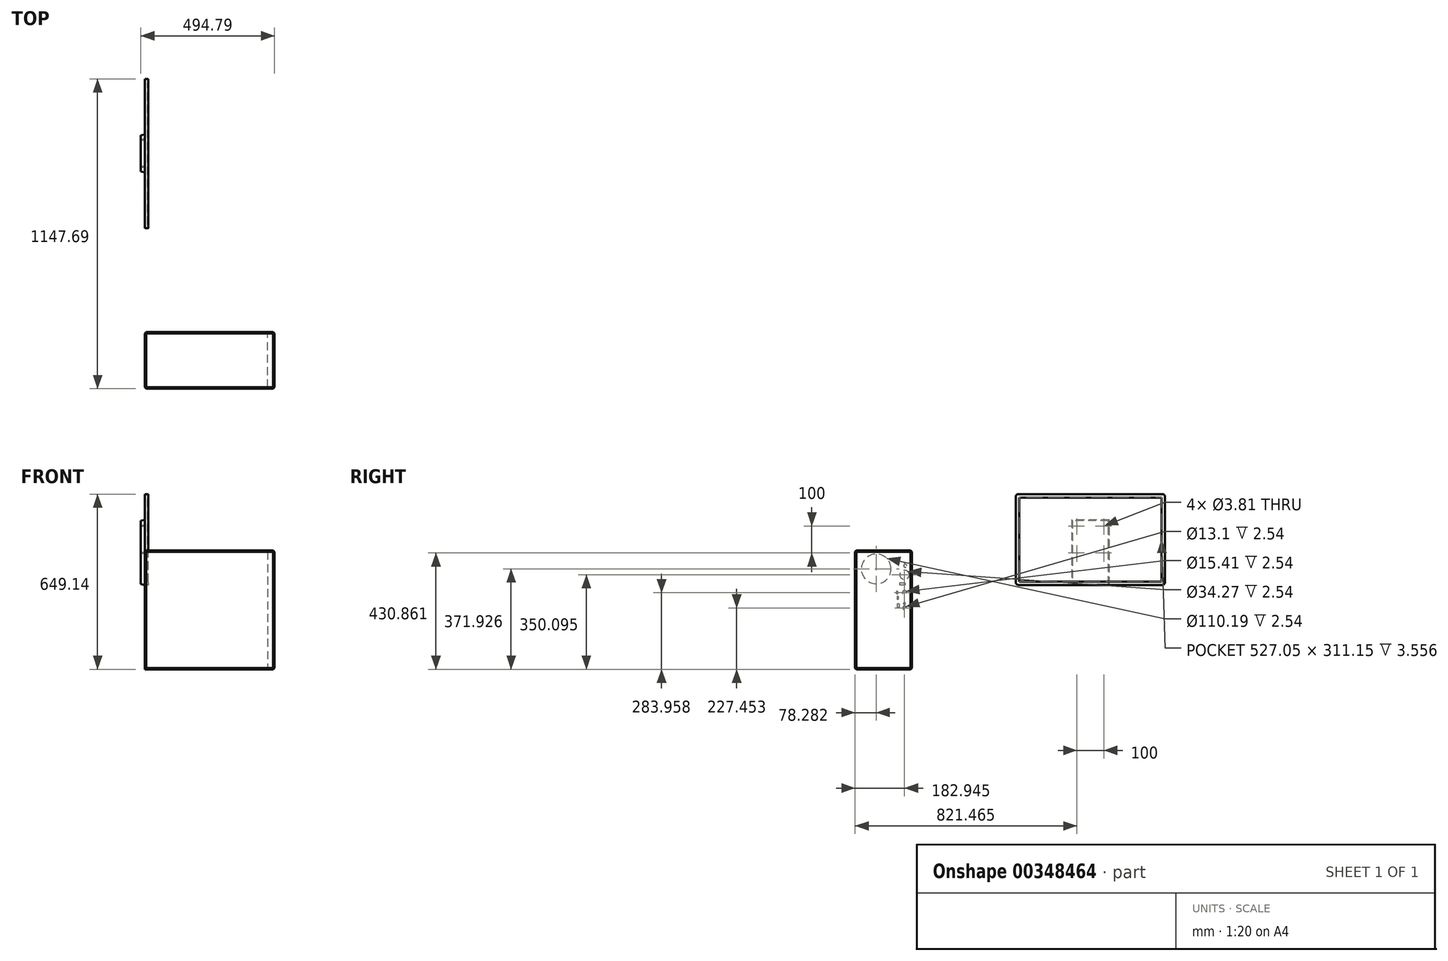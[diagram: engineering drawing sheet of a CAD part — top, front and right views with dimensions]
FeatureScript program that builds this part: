
annotation { "Feature Type Name" : "Feature", "Feature Type Description" : "" }
export const myFeature = defineFeature(function(context is Context, id is Id, definition is map)
    precondition{}
    {
        {
            var Q0;
            Q0=qCreatedBy(makeId("Top.planeOp"),FACE);
            var sketch = newSketch(context, id + "F0", { "sketchPlane" : qUnion([Q0])});
            skLineSegment(sketch, "E0.bottom", {"start": v(0, 0) * mm, "end": v(479.55, 0) * mm});
            skLineSegment(sketch, "E0.top", {"start": v(0, -210.06) * mm, "end": v(479.55, -210.06) * mm});
            skLineSegment(sketch, "E0.left", {"start": v(0, 0) * mm, "end": v(0, -210.06) * mm});
            skLineSegment(sketch, "E0.right", {"start": v(479.55, 0) * mm, "end": v(479.55, -210.06) * mm});
            skPoint(sketch, "E1", {"position": v(0, 0) * mm});
            skSolve(sketch);
        }
        {
            var Q0;
            Q0 = qSketchRegion(id + "F0", true);
            extrude(context, id + "F1", {"entities" : qUnion([Q0]), "depth" : 439.93 * mm});
        }
        {
            var Q0;
            Q0=makeQuery(id+"F1.opExtrude","CAP_FACE",FACE,{"disambiguationData":[OSD([sQuery(id+"F0.wireOp",EDGE,"E0.bottom"),sQuery(id+"F0.wireOp",EDGE,"E0.top"),sQuery(id+"F0.wireOp",EDGE,"E0.left"),sQuery(id+"F0.wireOp",EDGE,"E0.right")])],"isStart":false});
            var Q1;
            Q1=makeQuery(id+"F1.opExtrude","SWEPT_FACE",FACE,{"disambiguationData":[OSD([sQuery(id+"F0.wireOp",EDGE,"E0.top")])]});
            var Q2;
            Q2=makeQuery(id+"F1.opExtrude","SWEPT_FACE",FACE,{"disambiguationData":[OSD([sQuery(id+"F0.wireOp",EDGE,"E0.right")])]});
            var Q3;
            Q3=makeQuery(id+"F1.opExtrude","SWEPT_FACE",FACE,{"disambiguationData":[OSD([sQuery(id+"F0.wireOp",EDGE,"E0.bottom")])]});
            chamfer(context, id + "F2", {"entities" : qUnion([Q0, Q1, Q2, Q3]), "width" : 5.08 * mm, "tangentPropagation" : true});
        }
        {
            var Q0;
            Q0=makeQuery(id+"F1.opExtrude","SWEPT_FACE",FACE,{"disambiguationData":[OSD([sQuery(id+"F0.wireOp",EDGE,"E0.left")])]});
            var sketch = newSketch(context, id + "F3", { "sketchPlane" : qUnion([Q0])});
            skCircle(sketch, "E2", {"center": v(24.55, 383.48) * mm, "radius": 5.74 * mm});
            skCircle(sketch, "E3", {"center": v(27.12, 350.1) * mm, "radius": 17.13 * mm});
            skCircle(sketch, "E4", {"center": v(27.12, 283.96) * mm, "radius": 7.7 * mm});
            skCircle(sketch, "E5", {"center": v(27.12, 243.5) * mm, "radius": 3.9 * mm});
            skCircle(sketch, "E6", {"center": v(27.12, 227.45) * mm, "radius": 6.55 * mm});
            skLineSegment(sketch, "E7.bottom", {"start": v(24.55, 319.92) * mm, "end": v(45.1, 319.92) * mm});
            skLineSegment(sketch, "E7.top", {"start": v(24.55, 312.21) * mm, "end": v(45.1, 312.21) * mm});
            skLineSegment(sketch, "E7.left", {"start": v(24.55, 319.92) * mm, "end": v(24.55, 312.21) * mm});
            skLineSegment(sketch, "E7.right", {"start": v(45.1, 319.92) * mm, "end": v(45.1, 312.21) * mm});
            skLineSegment(sketch, "E8.bottom", {"start": v(53.44, 289.74) * mm, "end": v(57.3, 289.74) * mm});
            skLineSegment(sketch, "E8.top", {"start": v(53.44, 279.46) * mm, "end": v(57.3, 279.46) * mm});
            skLineSegment(sketch, "E8.left", {"start": v(53.44, 289.74) * mm, "end": v(53.44, 279.46) * mm});
            skLineSegment(sketch, "E8.right", {"start": v(57.3, 289.74) * mm, "end": v(57.3, 279.46) * mm});
            skLineSegment(sketch, "E9.bottom", {"start": v(50.23, 269.83) * mm, "end": v(54.08, 269.83) * mm});
            skLineSegment(sketch, "E9.top", {"start": v(50.23, 258.92) * mm, "end": v(54.08, 258.92) * mm});
            skLineSegment(sketch, "E9.left", {"start": v(50.23, 269.83) * mm, "end": v(50.23, 258.92) * mm});
            skLineSegment(sketch, "E9.right", {"start": v(54.08, 269.83) * mm, "end": v(54.08, 258.92) * mm});
            skLineSegment(sketch, "E10.bottom", {"start": v(47.02, 242.22) * mm, "end": v(54.08, 242.22) * mm});
            skLineSegment(sketch, "E10.top", {"start": v(47.02, 230.02) * mm, "end": v(54.08, 230.02) * mm});
            skLineSegment(sketch, "E10.left", {"start": v(47.02, 242.22) * mm, "end": v(47.02, 230.02) * mm});
            skLineSegment(sketch, "E10.right", {"start": v(54.08, 242.22) * mm, "end": v(54.08, 230.02) * mm});
            skCircle(sketch, "E11", {"center": v(131.78, 371.93) * mm, "radius": 55.1 * mm});
            skSolve(sketch);
        }
        {
            var Q0;
            Q0 = qSketchRegion(id + "F3", true);
            extrude(context, id + "F4", {"entities" : qUnion([Q0]), "operationType" : NewBodyOperationType.REMOVE, "oppositeDirection" : true, "depth" : 2.54 * mm});
        }
        {
            var Q0;
            Q0=makeQuery(id+"F1.opExtrude","SWEPT_FACE",FACE,{"disambiguationData":[OSD([sQuery(id+"F0.wireOp",EDGE,"E0.right")])]});
            extrude(context, id + "F5", {"entities" : qUnion([Q0]), "operationType" : NewBodyOperationType.REMOVE, "oppositeDirection" : true, "depth" : 25.4 * mm, "hasDraft" : true, "draftAngle" : 10 * degree});
        }
        {
            var Q0;
            Q0=qCreatedBy(makeId("Right.planeOp"),FACE);
            var sketch = newSketch(context, id + "F6", { "sketchPlane" : qUnion([Q0])});
            skLineSegment(sketch, "E12.bottom", {"start": v(385.18, 312.59) * mm, "end": v(937.63, 312.59) * mm});
            skLineSegment(sketch, "E12.top", {"start": v(385.18, 649.14) * mm, "end": v(937.63, 649.14) * mm});
            skLineSegment(sketch, "E12.left", {"start": v(385.18, 312.59) * mm, "end": v(385.18, 649.14) * mm});
            skLineSegment(sketch, "E12.right", {"start": v(937.63, 312.59) * mm, "end": v(937.63, 649.14) * mm});
            skSolve(sketch);
        }
        {
            var Q0;
            Q0 = qSketchRegion(id + "F6", true);
            extrude(context, id + "F7", {"entities" : qUnion([Q0]), "depth" : 12.7 * mm});
        }
        {
            var Q0;
            Q0=makeQuery(id+"F7.opExtrude","CAP_FACE",FACE,{"disambiguationData":[OSD([sQuery(id+"F6.wireOp",EDGE,"E12.bottom"),sQuery(id+"F6.wireOp",EDGE,"E12.top"),sQuery(id+"F6.wireOp",EDGE,"E12.left"),sQuery(id+"F6.wireOp",EDGE,"E12.right")])],"isStart":true});
            var sketch = newSketch(context, id + "F8", { "sketchPlane" : qUnion([Q0])});
            skLineSegment(sketch, "E13.bottom", {"start": v(-591.56, 312.59) * mm, "end": v(-731.26, 312.59) * mm});
            skLineSegment(sketch, "E13.top", {"start": v(-591.56, 553.89) * mm, "end": v(-731.26, 553.89) * mm});
            skLineSegment(sketch, "E13.left", {"start": v(-591.56, 312.59) * mm, "end": v(-591.56, 553.89) * mm});
            skLineSegment(sketch, "E13.right", {"start": v(-731.26, 312.59) * mm, "end": v(-731.26, 553.89) * mm});
            skLineSegment(sketch, "E14", {"start": v(-661.4, 312.59) * mm, "end": v(-661.4, 405.93) * mm, "construction": true});
            skSolve(sketch);
        }
        {
            var Q0;
            Q0=makeQuery(id+"F8.imprint","IMPRINT",FACE,{"disambiguationData":[TD([[makeQuery(id+"F8.imprint","IMPRINT",EDGE,{"derivedFrom":sQuery(id+"F8.wireOp",EDGE,"E13.bottom")}),-1.0]])]});
            extrude(context, id + "F9", {"entities" : qUnion([Q0]), "operationType" : NewBodyOperationType.ADD, "depth" : 15.24 * mm, "hasDraft" : true, "draftAngle" : 10 * degree, "draftPullDirection" : true});
        }
        {
            var Q0;
            Q0=makeQuery(id+"F7.opExtrude","CAP_FACE",FACE,{"disambiguationData":[OSD([sQuery(id+"F6.wireOp",EDGE,"E12.bottom"),sQuery(id+"F6.wireOp",EDGE,"E12.top"),sQuery(id+"F6.wireOp",EDGE,"E12.left"),sQuery(id+"F6.wireOp",EDGE,"E12.right")])],"isStart":false});
            var sketch = newSketch(context, id + "F10", { "sketchPlane" : qUnion([Q0])});
            skLineSegment(sketch, "E15.0", {"start": v(397.88, 325.29) * mm, "end": v(397.88, 636.44) * mm});
            skLineSegment(sketch, "E15.1", {"start": v(397.88, 325.29) * mm, "end": v(924.93, 325.29) * mm});
            skLineSegment(sketch, "E15.2", {"start": v(924.93, 325.29) * mm, "end": v(924.93, 636.44) * mm});
            skLineSegment(sketch, "E15.3", {"start": v(397.88, 636.44) * mm, "end": v(924.93, 636.44) * mm});
            skSolve(sketch);
        }
        {
            var Q0;
            Q0 = qSketchRegion(id + "F10", true);
            extrude(context, id + "F11", {"entities" : qUnion([Q0]), "operationType" : NewBodyOperationType.REMOVE, "oppositeDirection" : true, "depth" : 3.56 * mm});
        }
        {
            var Q0;
            Q0=makeQuery(id+"F7.opExtrude","SWEPT_EDGE",EDGE,{"disambiguationData":[OSD([sQuery(id+"F6.wireOp",EDGE,"E12.top"),sQuery(id+"F6.wireOp",EDGE,"E12.left")])]});
            var Q1;
            Q1=makeQuery(id+"F7.opExtrude","SWEPT_EDGE",EDGE,{"disambiguationData":[OSD([sQuery(id+"F6.wireOp",EDGE,"E12.top"),sQuery(id+"F6.wireOp",EDGE,"E12.right")])]});
            var Q2;
            Q2=makeQuery(id+"F7.opExtrude","SWEPT_EDGE",EDGE,{"disambiguationData":[OSD([sQuery(id+"F6.wireOp",EDGE,"E12.bottom"),sQuery(id+"F6.wireOp",EDGE,"E12.right")])]});
            var Q3;
            Q3=makeQuery(id+"F7.opExtrude","SWEPT_EDGE",EDGE,{"disambiguationData":[OSD([sQuery(id+"F6.wireOp",EDGE,"E12.bottom"),sQuery(id+"F6.wireOp",EDGE,"E12.left")])]});
            fillet(context, id + "F12", {"entities" : qUnion([Q0, Q1, Q2, Q3]), "radius" : 8.9 * mm, "tangentPropagation" : true, "allowEdgeOverflow" : false});
        }
        {
            var Q0;
            Q0=makeQuery(id+"F9.opExtrude","CAP_FACE",FACE,{"disambiguationData":[OSD([sQuery(id+"F8.wireOp",EDGE,"E13.bottom"),sQuery(id+"F8.wireOp",EDGE,"E13.top"),sQuery(id+"F8.wireOp",EDGE,"E13.left"),sQuery(id+"F8.wireOp",EDGE,"E13.right")])],"isStart":false});
            var sketch = newSketch(context, id + "F13", { "sketchPlane" : qUnion([Q0])});
            skLineSegment(sketch, "E16.bottom", {"start": v(-711.4, 430.86) * mm, "end": v(-611.4, 430.86) * mm, "construction": true});
            skLineSegment(sketch, "E16.top", {"start": v(-711.4, 530.86) * mm, "end": v(-611.4, 530.86) * mm, "construction": true});
            skLineSegment(sketch, "E16.left", {"start": v(-711.4, 430.86) * mm, "end": v(-711.4, 530.86) * mm, "construction": true});
            skLineSegment(sketch, "E16.right", {"start": v(-611.4, 430.86) * mm, "end": v(-611.4, 530.86) * mm, "construction": true});
            skLineSegment(sketch, "E17", {"start": v(-661.4, 649.14) * mm, "end": v(-661.4, 530.86) * mm, "construction": true});
            skPoint(sketch, "E17.endSnap0", {"position": v(-661.4, 551.2) * mm});
            skLineSegment(sketch, "E18", {"start": v(-661.4, 530.86) * mm, "end": v(-661.4, 430.86) * mm, "construction": true});
            skPoint(sketch, "E18.endSnap0", {"position": v(-661.4, 430.86) * mm});
            skLineSegment(sketch, "E19", {"start": v(-661.4, 430.86) * mm, "end": v(-661.4, 312.59) * mm, "construction": true});
            skSolve(sketch);
        }
        {
            var Q0;
            Q0=sQuery(id+"F13.wireOp",VERTEX,"E16.left.end");
            var Q1;
            Q1=sQuery(id+"F13.wireOp",VERTEX,"E16.bottom.start");
            var Q2;
            Q2=sQuery(id+"F13.wireOp",VERTEX,"E16.right.start");
            var Q3;
            Q3=sQuery(id+"F13.wireOp",VERTEX,"E16.top.end");
            var Q4;
            Q4=makeQuery(id+"F7.opExtrude","SWEPT_BODY",BODY,{"disambiguationData":[OSD([sQuery(id+"F6.wireOp",EDGE,"E12.bottom"),sQuery(id+"F6.wireOp",EDGE,"E12.top"),sQuery(id+"F6.wireOp",EDGE,"E12.left"),sQuery(id+"F6.wireOp",EDGE,"E12.right")])]});
            hole(context, id + "F14", {"style" : HoleStyle.SIMPLE, "endStyle" : HoleEndStyle.BLIND, "holeDiameter" : 3.8 * mm, "holeDepth" : 10.16 * mm, "isTappedThrough" : true, "tappedDepth" : 12.7 * mm, "tapClearance" : 3, "locations" : qUnion([Q0, Q1, Q2, Q3]), "scope" : qUnion([Q4])});
        }
    });
